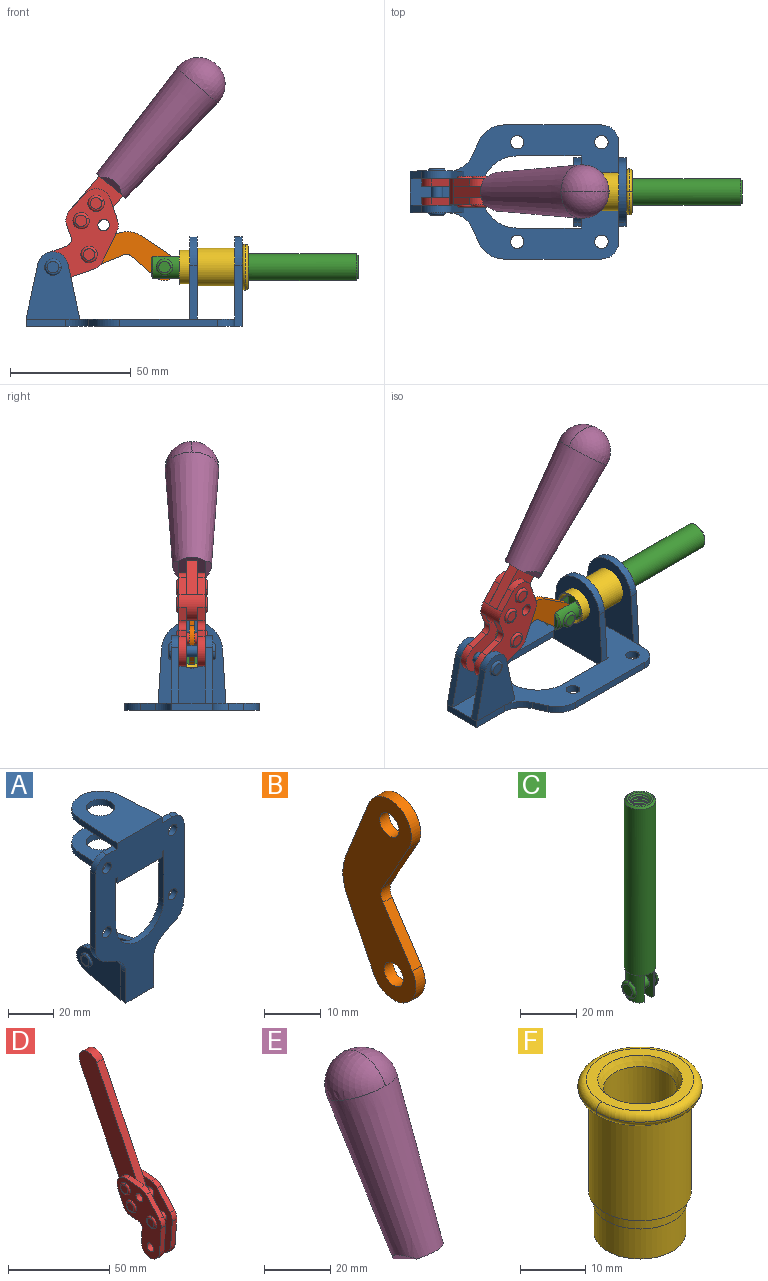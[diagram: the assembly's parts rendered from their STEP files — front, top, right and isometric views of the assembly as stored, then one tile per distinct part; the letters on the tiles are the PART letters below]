
ASSEMBLY  parts=6 mates=6
PART A: 55 faces, bbox 55.7x37.4x89.8 mm
  f0: torus R=2.41mm, axis (-1,0,0), area 15mm2, adj f11,f15,f25
  f1: torus R=2.41mm, axis (-1,0,0), area 15mm2, adj f10,f12,f22
  f2: cylinder r=2.78mm len=5.56mm, axis (0,-1,0), area 54.2mm2, adj f30,f54
  f3: cylinder r=14.99mm len=29.97mm, axis (0,-1,0), area 145.9mm2, adj f30,f49,f53,f54
  f4: cylinder r=2.78mm len=5.56mm, axis (0,-1,0), area 54.2mm2, adj f30,f54
  f5: cylinder r=2.78mm len=5.56mm, axis (0,-1,0), area 54.2mm2, adj f30,f54
  f6: cylinder r=2.78mm len=5.56mm, axis (0,-1,0), area 54.2mm2, adj f30,f54
  f7: cylinder r=6.35mm len=12.7mm, axis (0,0,1), area 123.6mm2, adj f27,f51
  f8: cylinder r=6.35mm len=12.7mm, axis (0,0,-1), area 124.7mm2, adj f21,f35
  f9: cylinder r=2.41mm len=11.18mm, axis (-1,0,0), area 169.4mm2, adj f16,f19
  f10: plane 4.83x4.83mm, normal (1,0,0), area 18.3mm2, adj f1,f12
  f11: plane 4.83x4.83mm, normal (-1,0,0), area 18.3mm2, adj f0,f15
  f12: torus R=2.41mm, axis (-1,0,0), area 15mm2, adj f1,f10,f22
  f13: cylinder r=6.35mm len=12.41mm, axis (1,0,0), area 53.4mm2, adj f18,f19,f22,f23
  f14: cylinder r=6.35mm len=12.41mm, axis (-1,0,0), area 53.4mm2, adj f16,f17,f24,f25
  f15: torus R=2.41mm, axis (-1,0,0), area 15mm2, adj f0,f11,f25
  f16: plane 27.86x22.35mm, normal (1,0,0), area 425.4mm2, adj f9,f14,f17,f24,f30
  f17: plane 22.86x4.97mm, normal (0,0.21,0.98), area 72.5mm2, adj f14,f16,f25,f30
  f18: plane 22.86x4.97mm, normal (0,0.21,0.98), area 72.5mm2, adj f13,f19,f22,f30
  f19: plane 27.86x22.35mm, normal (-1,0,0), area 425.4mm2, adj f9,f13,f18,f23,f30
  f20: cylinder r=12.7mm len=25.35mm, axis (0,0,-1), area 119.8mm2, adj f21,f34,f35,f36
  f21: plane 34.21x28.07mm, normal (0,0,-1), area 702.4mm2, adj f8,f20,f30,f34,f36
  f22: plane 27.96x22.45mm, normal (1,0,0), area 407.2mm2, adj f1,f12,f13,f18,f23,f30,f42,f43
  f23: plane 22.86x4.97mm, normal (0,0.21,-0.98), area 72.5mm2, adj f13,f19,f22,f44
  f24: plane 22.86x4.97mm, normal (0,0.21,-0.98), area 72.5mm2, adj f14,f16,f25,f44
  f25: plane 27.86x22.35mm, normal (-1,0,0), area 407.1mm2, adj f0,f14,f15,f17,f24,f30,f45,f46
  f26: plane 3.1x0.95mm, normal (0,0,-1), area 2.7mm2, adj f30,f49,f50,f54
  f27: plane 34.21x28.07mm, normal (0,0,1), area 702.4mm2, adj f7,f28,f30,f50,f52
  f28: cylinder r=12.7mm len=25.35mm, axis (0,0,1), area 118.8mm2, adj f27,f50,f51,f52
  f29: plane 3.1x0.95mm, normal (0,0,-1), area 2.7mm2, adj f30,f52,f53,f54
  f30: plane 86.54x55.63mm, normal (0,1,0), area 2362.9mm2, adj f2,f3,f4,f5,f6,f16,f17,f18
  f31: plane 40.56x3.1mm, normal (-1,0,0), area 125.7mm2, adj f30,f32,f48,f54
  f32: cylinder r=7.11mm len=7.11mm, axis (0,-1,0), area 34.6mm2, adj f30,f31,f33,f54
  f33: plane 6.67x3.1mm, normal (0,0,1), area 20.4mm2, adj f30,f32,f34,f54
  f34: plane 25.39x3.13mm, normal (-1,0.06,0), area 79.5mm2, adj f20,f21,f33,f35,f54
  f35: plane 37.31x28.45mm, normal (0,0,1), area 789.9mm2, adj f8,f20,f34,f36,f54
  f36: plane 25.39x3.13mm, normal (1,0.06,0), area 79.5mm2, adj f20,f21,f35,f37,f54
  f37: plane 6.67x3.1mm, normal (0,0,1), area 20.4mm2, adj f30,f36,f38,f54
  f38: cylinder r=7.11mm len=7.11mm, axis (0,-1,0), area 34.6mm2, adj f30,f37,f39,f54
  f39: plane 40.56x3.1mm, normal (1,0,0), area 125.7mm2, adj f30,f38,f40,f54
  f40: cylinder r=11.18mm len=10.16mm, axis (0,-1,0), area 39.5mm2, adj f30,f39,f41,f54
  f41: plane 6.09x3.1mm, normal (0.42,0,-0.91), area 20.8mm2, adj f30,f40,f42,f54
  f42: cylinder r=11.18mm len=9.41mm, axis (0,-1,0), area 37.2mm2, adj f22,f30,f41,f43,f54
  f43: plane 16.5x3.1mm, normal (1,0,0), area 51.1mm2, adj f22,f42,f44,f54
  f44: plane 17.37x3.1mm, normal (0,0,-1), area 53.8mm2, adj f23,f24,f30,f43,f45,f54
  f45: plane 16.5x3.1mm, normal (-1,0,0), area 51.1mm2, adj f25,f44,f46,f54
  f46: cylinder r=11.18mm len=9.41mm, axis (0,-1,0), area 37.2mm2, adj f25,f30,f45,f47,f54
  f47: plane 6.09x3.1mm, normal (-0.42,0,-0.91), area 20.8mm2, adj f30,f46,f48,f54
  f48: cylinder r=11.18mm len=10.16mm, axis (0,-1,0), area 39.5mm2, adj f30,f31,f47,f54
  f49: plane 26.54x3.1mm, normal (-1,0,0), area 82.3mm2, adj f3,f26,f30,f54
  f50: plane 25.39x3.1mm, normal (1,0.06,0), area 78.8mm2, adj f26,f27,f28,f51,f54
  f51: plane 37.31x28.45mm, normal (0,0,-1), area 789.9mm2, adj f7,f28,f50,f52,f54
  f52: plane 25.39x3.1mm, normal (-1,0.06,0), area 78.8mm2, adj f27,f28,f29,f51,f54
  f53: plane 26.54x3.1mm, normal (1,0,0), area 82.3mm2, adj f3,f29,f30,f54
  f54: plane 89.66x55.63mm, normal (0,-1,0), area 2678.5mm2, adj f2,f3,f4,f5,f6,f26,f29,f31
PART B: 12 faces, bbox 2.3x18.2x42.8 mm
  f0: cylinder r=2.4mm len=4.8mm, axis (1,0,0), area 34.9mm2, adj f4,f11
  f1: cylinder r=10.41mm len=8.47mm, axis (1,0,0), area 20.2mm2, adj f4,f9,f10,f11
  f2: cylinder r=3.05mm len=3.16mm, axis (1,0,0), area 7.7mm2, adj f4,f6,f7,f11
  f3: cylinder r=2.4mm len=4.8mm, axis (1,0,0), area 34.9mm2, adj f4,f11
  f4: plane 42.81x18.23mm, normal (-1,0,0), area 414.1mm2, adj f0,f1,f2,f3,f5,f6,f7,f8
  f5: cylinder r=5.54mm len=10.67mm, axis (1,0,0), area 41.8mm2, adj f4,f6,f10,f11
  f6: plane 11.66x6.53mm, normal (0,-0.87,-0.49), area 30.9mm2, adj f2,f4,f5,f11
  f7: plane 11.17x7.33mm, normal (0,-0.84,0.55), area 30.9mm2, adj f2,f4,f8,f11
  f8: cylinder r=5.54mm len=10.51mm, axis (1,0,0), area 41.8mm2, adj f4,f7,f9,f11
  f9: plane 13.67x6.67mm, normal (0,0.9,-0.44), area 35.1mm2, adj f1,f4,f8,f11
  f10: plane 14.1x5.7mm, normal (0,0.93,0.37), area 35.1mm2, adj f1,f4,f5,f11
  f11: plane 42.81x18.23mm, normal (1,0,0), area 414.1mm2, adj f0,f1,f2,f3,f5,f6,f7,f8
PART C: 48 faces, bbox 12.6x11.1x86.1 mm
  f0: torus R=2.41mm, axis (-1,0,0), area 15mm2, adj f30,f32,f34
  f1: torus R=2.41mm, axis (-1,0,0), area 15mm2, adj f29,f31,f33
  f2: cylinder r=5.54mm len=72.39mm, axis (0,0,1), area 2518.5mm2, adj f3,f4,f42,f43
  f3: cone r=5.54mm half-angle=45deg, axis (0,0,1), area 7.6mm2, adj f2,f5,f41
  f4: cone r=5.54mm half-angle=45deg, axis (0,0,-1), area 34.9mm2, adj f2,f39
  f5: cylinder r=5.08mm len=11.48mm, axis (0,0,1), area 108.3mm2, adj f3,f7,f8,f41
  f6: cylinder r=2.41mm len=4.83mm, axis (-1,0,0), area 71.2mm2, adj f40,f41
  f7: cylinder r=2.41mm len=4.83mm, axis (-1,0,0), area 7.6mm2, adj f5,f34
  f8: cone r=5.08mm half-angle=45deg, axis (0,0,1), area 10.6mm2, adj f5,f37,f41
  f9: cone r=3.98mm half-angle=45deg, axis (0,0,1), area 17.6mm2, adj f27,f39,f45,f46,f47
  f10: cylinder r=2.41mm len=4.83mm, axis (-1,0,0), area 7.6mm2, adj f33,f38
  f11: cylinder r=3.2mm len=6.4mm, axis (0,0,1), area 78.4mm2, adj f12,f28,f44,f45,f47
  f12: cylinder r=3.2mm len=6.4mm, axis (0,0,1), area 10.5mm2, adj f11,f13,f45,f47
  f13: cylinder r=3.2mm len=6.4mm, axis (0,0,1), area 10.5mm2, adj f12,f14,f45,f47
  f14: cylinder r=3.2mm len=6.4mm, axis (0,0,1), area 10.5mm2, adj f13,f15,f45,f47
  f15: cylinder r=3.2mm len=6.4mm, axis (0,0,1), area 10.5mm2, adj f14,f16,f45,f47
  f16: cylinder r=3.2mm len=6.4mm, axis (0,0,1), area 10.5mm2, adj f15,f17,f45,f47
  f17: cylinder r=3.2mm len=6.4mm, axis (0,0,1), area 10.5mm2, adj f16,f18,f45,f47
  f18: cylinder r=3.2mm len=6.4mm, axis (0,0,1), area 10.5mm2, adj f17,f19,f45,f47
  f19: cylinder r=3.2mm len=6.4mm, axis (0,0,1), area 10.5mm2, adj f18,f20,f45,f47
  f20: cylinder r=3.2mm len=6.4mm, axis (0,0,1), area 10.5mm2, adj f19,f21,f45,f47
  f21: cylinder r=3.2mm len=6.4mm, axis (0,0,1), area 10.5mm2, adj f20,f22,f45,f47
  f22: cylinder r=3.2mm len=6.4mm, axis (0,0,1), area 10.5mm2, adj f21,f23,f45,f47
  f23: cylinder r=3.2mm len=6.4mm, axis (0,0,1), area 10.5mm2, adj f22,f24,f45,f47
  f24: cylinder r=3.2mm len=6.4mm, axis (0,0,1), area 10.5mm2, adj f23,f25,f45,f47
  f25: cylinder r=3.2mm len=6.4mm, axis (0,0,1), area 10.5mm2, adj f24,f26,f45,f47
  f26: cylinder r=3.2mm len=6.4mm, axis (0,0,1), area 10.5mm2, adj f25,f27,f45,f47
  f27: cylinder r=3.2mm len=6.4mm, axis (0,0,1), area 7.4mm2, adj f9,f26,f45,f47
  f28: cone r=3.2mm half-angle=60deg, axis (0,0,1), area 37.2mm2, adj f11
  f29: plane 4.83x4.83mm, normal (-1,0,0), area 18.3mm2, adj f1,f31
  f30: plane 4.83x4.83mm, normal (1,0,0), area 18.3mm2, adj f0,f32
  f31: torus R=2.41mm, axis (-1,0,0), area 15mm2, adj f1,f29,f33
  f32: torus R=2.41mm, axis (-1,0,0), area 15mm2, adj f0,f30,f34
  f33: plane 6.83x6.83mm, normal (1,0,0), area 18.3mm2, adj f1,f10,f31
  f34: plane 6.83x6.83mm, normal (-1,0,0), area 18.3mm2, adj f0,f7,f32
  f35: cone r=5.08mm half-angle=45deg, axis (0,0,1), area 10.6mm2, adj f36,f38,f40
  f36: plane 7.25x1.97mm, normal (0,0,-1), area 10mm2, adj f35,f40
  f37: plane 7.25x1.97mm, normal (0,0,-1), area 10mm2, adj f8,f41
  f38: cylinder r=5.08mm len=11.48mm, axis (0,0,1), area 108.3mm2, adj f10,f35,f40,f42
  f39: plane 9.55x9.55mm, normal (0,0,1), area 22mm2, adj f4,f9
  f40: plane 12.76x10.09mm, normal (1,0,0), area 95.7mm2, adj f6,f35,f36,f38,f42,f43
  f41: plane 12.76x10.09mm, normal (-1,0,0), area 95.7mm2, adj f3,f5,f6,f8,f37,f43
  f42: cone r=5.54mm half-angle=45deg, axis (0,0,1), area 7.6mm2, adj f2,f38,f40
  f43: plane 11.07x4.7mm, normal (0,0,-1), area 50.4mm2, adj f2,f40,f41
  f44: plane 0.89x0.62mm, normal (-1,0,0), area 0.3mm2, adj f11,f45,f46,f47
  f45: bspline ~24.8x7.63mm, area 266.6mm2, adj f9,f11,f12,f13,f14,f15,f16,f17
  f46: bspline ~24.87x7.63mm, area 73.6mm2, adj f9,f44,f45,f47
  f47: bspline ~24.98x7.63mm, area 272.5mm2, adj f9,f11,f12,f13,f14,f15,f16,f17
PART D: 59 faces, bbox 12.9x60.2x99.6 mm
  f0: torus R=2.39mm, axis (-1,0,0), area 14.9mm2, adj f20,f43,f51
  f1: torus R=2.39mm, axis (-1,0,0), area 14.9mm2, adj f19,f42,f51
  f2: torus R=2.39mm, axis (-1,0,0), area 14.9mm2, adj f18,f35,f51
  f3: torus R=2.39mm, axis (-1,0,0), area 14.9mm2, adj f14,f17,f23
  f4: torus R=2.39mm, axis (-1,0,0), area 14.9mm2, adj f13,f16,f23
  f5: torus R=2.39mm, axis (-1,0,0), area 14.9mm2, adj f12,f15,f23
  f6: cylinder r=2.39mm len=4.78mm, axis (1,0,0), area 46.5mm2, adj f48,f50,f51
  f7: cylinder r=2.39mm len=4.78mm, axis (1,0,0), area 46.5mm2, adj f50,f51
  f8: cylinder r=6.35mm len=12.68mm, axis (1,0,0), area 61.8mm2, adj f38,f39,f50,f51
  f9: cylinder r=2.39mm len=4.78mm, axis (-1,0,0), area 70.5mm2, adj f46,f50
  f10: cylinder r=2.39mm len=4.78mm, axis (-1,0,0), area 46.5mm2, adj f23,f45,f46
  f11: cylinder r=2.39mm len=4.78mm, axis (-1,0,0), area 46.5mm2, adj f23,f46
  f12: plane 4.78x4.78mm, normal (1,0,0), area 17.9mm2, adj f5,f15
  f13: plane 4.78x4.78mm, normal (1,0,0), area 17.9mm2, adj f4,f16
  f14: plane 4.78x4.78mm, normal (1,0,0), area 17.9mm2, adj f3,f17
  f15: torus R=2.39mm, axis (-1,0,0), area 14.9mm2, adj f5,f12,f23
  f16: torus R=2.39mm, axis (-1,0,0), area 14.9mm2, adj f4,f13,f23
  f17: torus R=2.39mm, axis (-1,0,0), area 14.9mm2, adj f3,f14,f23
  f18: plane 4.78x4.78mm, normal (-1,0,0), area 17.9mm2, adj f2,f35
  f19: plane 4.78x4.78mm, normal (-1,0,0), area 17.9mm2, adj f1,f42
  f20: plane 4.78x4.78mm, normal (-1,0,0), area 17.9mm2, adj f0,f43
  f21: plane 2.26x0.2mm, normal (1,0,0), area 0.2mm2, adj f31,f44
  f22: plane 2.26x0.2mm, normal (-1,0,0), area 0.2mm2, adj f41,f44
  f23: plane 39.37x30.77mm, normal (1,0,0), area 565.5mm2, adj f3,f4,f5,f10,f11,f15,f16,f17
  f24: cylinder r=6.1mm len=4.15mm, axis (-1,0,0), area 14.7mm2, adj f23,f25,f32,f46
  f25: plane 10.25x9.01mm, normal (0,-0.75,0.66), area 42.3mm2, adj f23,f24,f26,f46
  f26: cylinder r=6.35mm len=4.64mm, axis (-1,0,0), area 15.6mm2, adj f23,f25,f27,f46
  f27: plane 15.84x3.1mm, normal (0,-1,-0.07), area 49.2mm2, adj f23,f26,f28,f46
  f28: cylinder r=6.35mm len=12.68mm, axis (-1,0,0), area 61.8mm2, adj f23,f27,f29,f46
  f29: plane 8.11x3.1mm, normal (0,1,0.07), area 25.2mm2, adj f23,f28,f30,f46
  f30: cylinder r=3.05mm len=3.25mm, axis (-1,0,0), area 14.8mm2, adj f23,f29,f31,f46
  f31: plane 5.99x3.1mm, normal (0,0.07,-1), area 18.6mm2, adj f21,f23,f30,f44,f46
  f32: plane 9.5x3.1mm, normal (0,-0.07,1), area 29.5mm2, adj f23,f24,f33,f46,f47
  f33: cylinder r=6.1mm len=8.63mm, axis (-1,0,0), area 39.1mm2, adj f23,f32,f34,f47
  f34: plane 8.65x3.96mm, normal (0,0.91,-0.42), area 29.5mm2, adj f23,f33,f44,f47
  f35: torus R=2.39mm, axis (-1,0,0), area 14.9mm2, adj f2,f18,f51
  f36: plane 10.25x9.01mm, normal (0,-0.75,0.66), area 42.3mm2, adj f37,f49,f50,f51
  f37: cylinder r=6.35mm len=4.64mm, axis (1,0,0), area 15.6mm2, adj f36,f38,f50,f51
  f38: plane 15.84x3.1mm, normal (0,-1,-0.07), area 49.2mm2, adj f8,f37,f50,f51
  f39: plane 8.11x3.1mm, normal (0,1,0.07), area 25.2mm2, adj f8,f40,f50,f51
  f40: cylinder r=3.05mm len=3.25mm, axis (1,0,0), area 14.8mm2, adj f39,f41,f50,f51
  f41: plane 5.99x3.1mm, normal (0,0.07,-1), area 18.6mm2, adj f22,f40,f44,f50,f51
  f42: torus R=2.39mm, axis (-1,0,0), area 14.9mm2, adj f1,f19,f51
  f43: torus R=2.39mm, axis (-1,0,0), area 14.9mm2, adj f0,f20,f51
  f44: cylinder r=6.35mm len=12.12mm, axis (-1,0,0), area 128.9mm2, adj f21,f22,f23,f31,f34,f41,f46,f47
  f45: plane 2.65x1.35mm, normal (1,0,0), area 1mm2, adj f10,f55
  f46: plane 39.08x20.42mm, normal (-1,0,0), area 412.5mm2, adj f9,f10,f11,f24,f25,f26,f27,f28
  f47: plane 77.62x39.82mm, normal (1,0,0), area 850mm2, adj f32,f33,f34,f44,f53,f54,f55
  f48: plane 2.65x1.35mm, normal (-1,0,0), area 1mm2, adj f6,f55
  f49: cylinder r=6.1mm len=4.15mm, axis (1,0,0), area 14.7mm2, adj f36,f50,f51,f56
  f50: plane 39.08x20.42mm, normal (1,0,0), area 412.5mm2, adj f6,f7,f8,f9,f36,f37,f38,f39
  f51: plane 39.37x30.77mm, normal (-1,0,0), area 565.5mm2, adj f0,f1,f2,f6,f7,f8,f35,f36
  f52: plane 8.65x3.96mm, normal (0,0.91,-0.42), area 29.5mm2, adj f44,f51,f57,f58
  f53: plane 68.49x33.4mm, normal (0,0.9,-0.44), area 358.1mm2, adj f44,f47,f54,f58
  f54: cylinder r=6.35mm len=12.06mm, axis (1,0,0), area 93.7mm2, adj f47,f53,f55,f58
  f55: plane 68.49x33.4mm, normal (0,-0.9,0.44), area 358.1mm2, adj f44,f45,f46,f47,f48,f50,f54,f58
  f56: plane 9.5x3.1mm, normal (0,-0.07,1), area 29.5mm2, adj f49,f50,f51,f57,f58
  f57: cylinder r=6.1mm len=8.63mm, axis (1,0,0), area 39.1mm2, adj f51,f52,f56,f58
  f58: plane 77.62x39.82mm, normal (-1,0,0), area 850mm2, adj f44,f52,f53,f54,f55,f56,f57
PART E: 11 faces, bbox 22.3x42.6x64.5 mm
  f0: sphere r=11.13mm, area 411.4mm2, adj f1,f8
  f1: cone r=11.11mm half-angle=3.3deg, axis (0,0.44,0.9), area 3251.8mm2, adj f0,f7,f8,f9,f10
  f2: cylinder r=6.16mm len=11.7mm, axis (1,0,0), area 89.5mm2, adj f3,f4,f5,f6
  f3: plane 60.23x36.75mm, normal (-1,0,0), area 763.6mm2, adj f2,f4,f6,f10
  f4: plane 51.37x25.05mm, normal (0,0.9,-0.44), area 264.2mm2, adj f2,f3,f5,f10
  f5: plane 60.23x36.75mm, normal (1,0,0), area 763.6mm2, adj f2,f4,f6,f10
  f6: plane 51.37x25.05mm, normal (0,-0.9,0.44), area 264.2mm2, adj f2,f3,f5,f10
  f7: plane 9.95x5.95mm, normal (0.71,-0.31,-0.64), area 25.8mm2, adj f1,f10
  f8: sphere r=11.13mm, area 411.4mm2, adj f0,f1
  f9: plane 9.95x5.95mm, normal (-0.71,-0.31,-0.64), area 25.8mm2, adj f1,f10
  f10: plane 14.27x11.38mm, normal (0,-0.44,-0.9), area 106.7mm2, adj f1,f3,f4,f5,f6,f7,f9
PART F: 15 faces, bbox 20.6x20.6x28.7 mm
  f0: torus R=8.26mm, axis (0,0,1), area 56.8mm2, adj f1,f10,f12
  f1: torus R=8.26mm, axis (0,0,1), area 56.8mm2, adj f0,f6,f13
  f2: cylinder r=5.59mm len=25.91mm, axis (0,0,1), area 909.6mm2, adj f3,f4
  f3: cone r=6.86mm half-angle=45deg, axis (0,0,-1), area 70.2mm2, adj f2,f14
  f4: cone r=6.47mm half-angle=30deg, axis (0,0,1), area 66.7mm2, adj f2,f13
  f5: cylinder r=7.04mm len=14.07mm, axis (0,0,1), area 252.6mm2, adj f11,f14
  f6: torus R=8.26mm, axis (0,0,1), area 56.8mm2, adj f1,f12,f13
  f7: cylinder r=7.16mm len=14.33mm, axis (0,0,1), area 91.5mm2, adj f9,f11
  f8: cylinder r=7.86mm len=18.42mm, axis (0,0,1), area 909.6mm2, adj f9,f10
  f9: plane 15.72x15.72mm, normal (0,0,-1), area 33mm2, adj f7,f8
  f10: plane 16.51x16.51mm, normal (0,0,-1), area 19.9mm2, adj f0,f8,f12
  f11: plane 14.33x14.33mm, normal (0,0,-1), area 5.7mm2, adj f5,f7
  f12: torus R=8.26mm, axis (0,0,1), area 56.8mm2, adj f0,f6,f10
  f13: plane 16.51x16.51mm, normal (0,0,1), area 82.7mm2, adj f1,f4,f6
  f14: plane 14.07x14.07mm, normal (0,0,-1), area 7.8mm2, adj f3,f5
PLACE A rot(axis=(0.58,0.58,0.58),120deg) t=(0,37.64,-0.11)mm fixed
PLACE B rot(axis=(0.55,-0.55,-0.63),115.7deg) t=(-5.01,37.64,3.34)mm
PLACE C rot(axis=(-0.58,0.58,-0.58),120deg) t=(-1.28,37.64,49.12)mm
PLACE D rot(axis=(0.48,0.48,0.73),107.6deg) t=(7.13,37.64,14.64)mm
PLACE E rot(axis=(0.48,0.48,0.73),107.6deg) t=(7.13,37.64,14.64)mm
PLACE F rot(axis=(0.71,0,0.71),180deg) t=(0,62.25,24.51)mm
MATE revolute B.f5 <-> D.f4  axis (0,-1,0) through (-17.12,37.64,29.77)mm
MATE slider F.f2 <-> C.f2  axis (1,0,0) through (47.41,37.64,24.51)mm
MATE fastened E.f2 <-> D.f54  axis (0,1,0) through (29.24,37.64,101.58)mm
MATE revolute D.f7 <-> A.f0  axis (0,-1,0) through (-32.09,37.64,24.51)mm
MATE revolute C.f6 <-> B.f3  axis (0,1,0) through (14.19,37.64,24.51)mm
MATE fastened F.f2 <-> A.f7  axis (-1,0,0) through (46.39,37.64,24.51)mm
